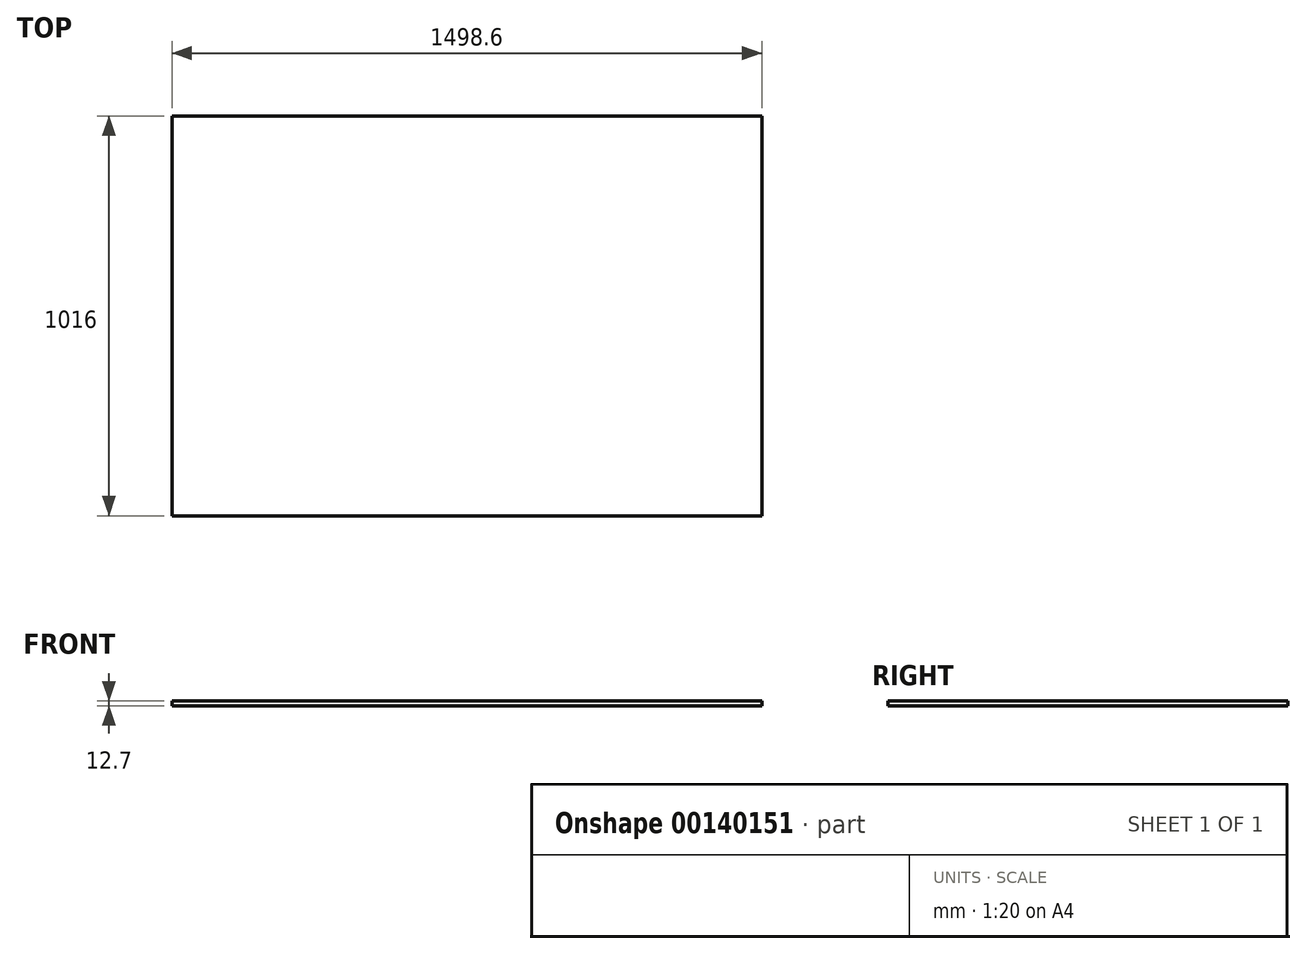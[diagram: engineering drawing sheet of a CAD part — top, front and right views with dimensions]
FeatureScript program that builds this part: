
annotation { "Feature Type Name" : "Feature", "Feature Type Description" : "" }
export const myFeature = defineFeature(function(context is Context, id is Id, definition is map)
    precondition{}
    {
        {
            var Q0;
            Q0=qCreatedBy(makeId("Front.planeOp"),FACE);
            var sketch = newSketch(context, id + "F0", { "sketchPlane" : qUnion([Q0])});
            skLineSegment(sketch, "E0", {"start": v(-749.3, 749.3) * mm, "end": v(-749.3, 762) * mm});
            skLineSegment(sketch, "E1", {"start": v(-749.3, 762) * mm, "end": v(749.3, 762) * mm});
            skLineSegment(sketch, "E2", {"start": v(749.3, 762) * mm, "end": v(749.3, 749.3) * mm});
            skLineSegment(sketch, "E3", {"start": v(-749.3, 749.3) * mm, "end": v(749.3, 749.3) * mm});
            skSolve(sketch);
        }
        {
            var Q0;
            Q0=makeQuery(id+"F0.imprint","IMPRINT",FACE,{"disambiguationData":[TD([[makeQuery(id+"F0.imprint","IMPRINT",EDGE,{"derivedFrom":sQuery(id+"F0.wireOp",EDGE,"E0")}),-1.0]])]});
            extrude(context, id + "F1", {"entities" : qUnion([Q0]), "depth" : 1016 * mm});
        }
    });
